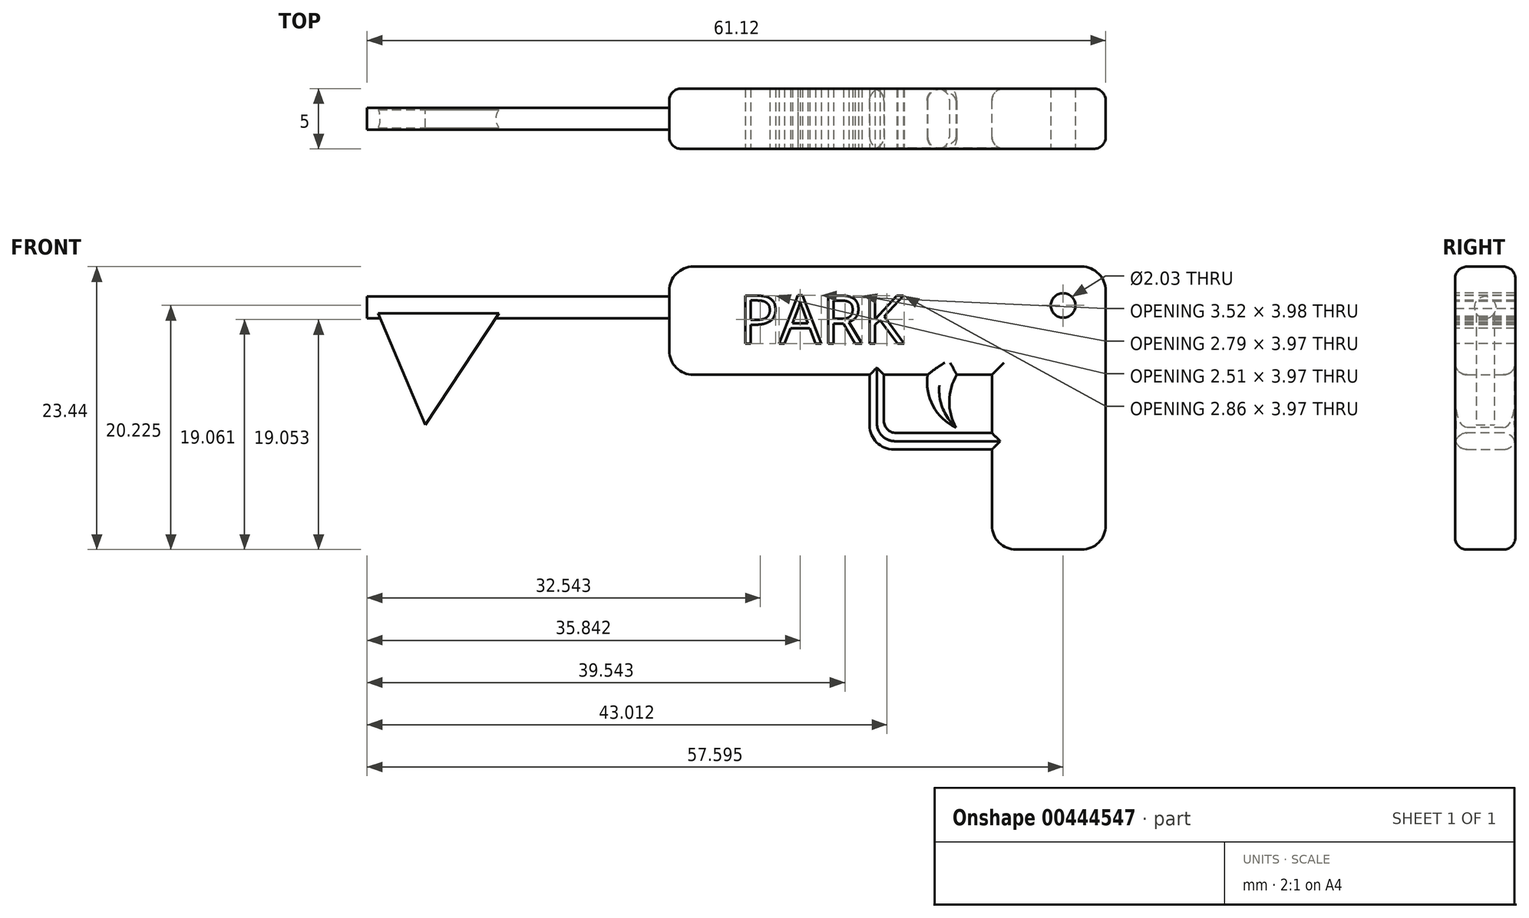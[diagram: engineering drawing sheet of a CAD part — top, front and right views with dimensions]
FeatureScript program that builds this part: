
annotation { "Feature Type Name" : "Feature", "Feature Type Description" : "" }
export const myFeature = defineFeature(function(context is Context, id is Id, definition is map)
    precondition{}
    {
        {
            var Q0;
            Q0=qCreatedBy(makeId("Front.planeOp"),FACE);
            var sketch = newSketch(context, id + "F0", { "sketchPlane" : qUnion([Q0])});
            skLineSegment(sketch, "E0", {"start": v(7.32, -12.37) * mm, "end": v(12.73, -12.37) * mm});
            skLineSegment(sketch, "E1", {"start": v(14.73, -10.37) * mm, "end": v(14.73, 9.07) * mm});
            skLineSegment(sketch, "E2", {"start": v(12.73, 11.07) * mm, "end": v(-19.39, 11.07) * mm});
            skLineSegment(sketch, "E3", {"start": v(-21.39, 9.07) * mm, "end": v(-21.39, 4.1) * mm});
            skLineSegment(sketch, "E4", {"start": v(-19.39, 2.1) * mm, "end": v(-4.8, 2.1) * mm});
            skLineSegment(sketch, "E5", {"start": v(-4.8, 2.1) * mm, "end": v(-4.8, -2.08) * mm});
            skLineSegment(sketch, "E6", {"start": v(-2.8, -4.08) * mm, "end": v(5.32, -4.08) * mm});
            skLineSegment(sketch, "E7", {"start": v(5.32, -4.08) * mm, "end": v(5.32, -10.37) * mm});
            skPoint(sketch, "E8.visualSharp", {"position": v(-21.39, 11.07) * mm});
            skArc(sketch, "E8.filletArc", {"start": v(-19.39, 11.07) * mm, "mid": v(-20.8, 10.48) * mm, "end": v(-21.39, 9.07) * mm});
            skPoint(sketch, "E9.visualSharp", {"position": v(-21.39, 2.1) * mm});
            skArc(sketch, "E9.filletArc", {"start": v(-21.39, 4.1) * mm, "mid": v(-20.8, 2.7) * mm, "end": v(-19.39, 2.1) * mm});
            skPoint(sketch, "E10.visualSharp", {"position": v(14.73, 11.07) * mm});
            skArc(sketch, "E10.filletArc", {"start": v(14.73, 9.07) * mm, "mid": v(14.15, 10.48) * mm, "end": v(12.73, 11.07) * mm});
            skPoint(sketch, "E11.visualSharp", {"position": v(14.73, -12.37) * mm});
            skArc(sketch, "E11.filletArc", {"start": v(12.73, -12.37) * mm, "mid": v(14.15, -11.78) * mm, "end": v(14.73, -10.37) * mm});
            skPoint(sketch, "E12.visualSharp", {"position": v(5.32, -12.37) * mm});
            skArc(sketch, "E12.filletArc", {"start": v(5.32, -10.37) * mm, "mid": v(5.9, -11.78) * mm, "end": v(7.32, -12.37) * mm});
            skPoint(sketch, "E13.visualSharp", {"position": v(-4.8, -4.08) * mm});
            skArc(sketch, "E13.filletArc", {"start": v(-4.8, -2.08) * mm, "mid": v(-4.22, -3.49) * mm, "end": v(-2.8, -4.08) * mm});
            skSolve(sketch);
        }
        {
            var Q0;
            Q0 = qSketchRegion(id + "F0", true);
            extrude(context, id + "F1", {"entities" : qUnion([Q0]), "depth" : 5 * mm});
        }
        {
            var Q0;
            Q0=makeQuery(id+"F1.opExtrude","CAP_FACE",FACE,{"disambiguationData":[OSD([sQuery(id+"F0.wireOp",EDGE,"E0"),sQuery(id+"F0.wireOp",EDGE,"E1"),sQuery(id+"F0.wireOp",EDGE,"E2"),sQuery(id+"F0.wireOp",EDGE,"E3"),sQuery(id+"F0.wireOp",EDGE,"E4"),sQuery(id+"F0.wireOp",EDGE,"E5"),sQuery(id+"F0.wireOp",EDGE,"E6"),sQuery(id+"F0.wireOp",EDGE,"E7"),sQuery(id+"F0.wireOp",EDGE,"E8.filletArc"),sQuery(id+"F0.wireOp",EDGE,"E9.filletArc"),sQuery(id+"F0.wireOp",EDGE,"E10.filletArc"),sQuery(id+"F0.wireOp",EDGE,"E11.filletArc"),sQuery(id+"F0.wireOp",EDGE,"E12.filletArc"),sQuery(id+"F0.wireOp",EDGE,"E13.filletArc")])],"isStart":false});
            var sketch = newSketch(context, id + "F2", { "sketchPlane" : qUnion([Q0])});
            skLineSegment(sketch, "E14.bottom", {"start": v(-3.62, 2.1) * mm, "end": v(0, 2.1) * mm});
            skLineSegment(sketch, "E14.top", {"start": v(-2.62, -2.7) * mm, "end": v(5.32, -2.7) * mm});
            skLineSegment(sketch, "E14.left", {"start": v(-3.62, 2.1) * mm, "end": v(-3.62, -1.7) * mm});
            skLineSegment(sketch, "E14.right", {"start": v(5.32, 2.1) * mm, "end": v(5.32, -2.7) * mm});
            skPoint(sketch, "E15.visualSharp", {"position": v(-3.62, -2.7) * mm});
            skArc(sketch, "E15.filletArc", {"start": v(-3.62, -1.7) * mm, "mid": v(-3.33, -2.41) * mm, "end": v(-2.62, -2.7) * mm});
            skArc(sketch, "E16", {"start": v(2.4, 2.1) * mm, "mid": v(1.79, -0.06) * mm, "end": v(2.33, -2.26) * mm});
            skArc(sketch, "E17", {"start": v(0, 2.1) * mm, "mid": v(0.44, -0.47) * mm, "end": v(2.33, -2.26) * mm});
            skLineSegment(sketch, "E18.trimOffspring", {"start": v(2.4, 2.1) * mm, "end": v(5.32, 2.1) * mm});
            skSolve(sketch);
        }
        {
            var Q0;
            Q0 = qSketchRegion(id + "F2", true);
            extrude(context, id + "F3", {"entities" : qUnion([Q0]), "operationType" : NewBodyOperationType.REMOVE, "endBound" : BoundingType.THROUGH_ALL, "oppositeDirection" : true, "depth" : 25 * mm});
        }
        {
            var Q0;
            Q0=makeQuery(id+"F1.opExtrude","CAP_EDGE",EDGE,{"disambiguationData":[OSD([sQuery(id+"F0.wireOp",EDGE,"E2")])],"isStart":false});
            var Q1;
            Q1=makeQuery(id+"F1.opExtrude","CAP_FACE",FACE,{"disambiguationData":[OSD([sQuery(id+"F0.wireOp",EDGE,"E0"),sQuery(id+"F0.wireOp",EDGE,"E1"),sQuery(id+"F0.wireOp",EDGE,"E2"),sQuery(id+"F0.wireOp",EDGE,"E3"),sQuery(id+"F0.wireOp",EDGE,"E4"),sQuery(id+"F0.wireOp",EDGE,"E5"),sQuery(id+"F0.wireOp",EDGE,"E6"),sQuery(id+"F0.wireOp",EDGE,"E7"),sQuery(id+"F0.wireOp",EDGE,"E8.filletArc"),sQuery(id+"F0.wireOp",EDGE,"E9.filletArc"),sQuery(id+"F0.wireOp",EDGE,"E10.filletArc"),sQuery(id+"F0.wireOp",EDGE,"E11.filletArc"),sQuery(id+"F0.wireOp",EDGE,"E12.filletArc"),sQuery(id+"F0.wireOp",EDGE,"E13.filletArc")])],"isStart":true});
            var Q2;
            Q2=makeQuery(id+"F1.opExtrude","CAP_FACE",FACE,{"disambiguationData":[OSD([sQuery(id+"F0.wireOp",EDGE,"E0"),sQuery(id+"F0.wireOp",EDGE,"E1"),sQuery(id+"F0.wireOp",EDGE,"E2"),sQuery(id+"F0.wireOp",EDGE,"E3"),sQuery(id+"F0.wireOp",EDGE,"E4"),sQuery(id+"F0.wireOp",EDGE,"E5"),sQuery(id+"F0.wireOp",EDGE,"E6"),sQuery(id+"F0.wireOp",EDGE,"E7"),sQuery(id+"F0.wireOp",EDGE,"E8.filletArc"),sQuery(id+"F0.wireOp",EDGE,"E9.filletArc"),sQuery(id+"F0.wireOp",EDGE,"E10.filletArc"),sQuery(id+"F0.wireOp",EDGE,"E11.filletArc"),sQuery(id+"F0.wireOp",EDGE,"E12.filletArc"),sQuery(id+"F0.wireOp",EDGE,"E13.filletArc")])],"isStart":false});
            fillet(context, id + "F4", {"entities" : qUnion([Q0, Q1, Q2]), "radius" : 1 * mm, "tangentPropagation" : true, "allowEdgeOverflow" : false});
        }
        {
            var Q0;
            Q0=makeQuery(id+"F1.opExtrude","CAP_FACE",FACE,{"disambiguationData":[OSD([sQuery(id+"F0.wireOp",EDGE,"E0"),sQuery(id+"F0.wireOp",EDGE,"E1"),sQuery(id+"F0.wireOp",EDGE,"E2"),sQuery(id+"F0.wireOp",EDGE,"E3"),sQuery(id+"F0.wireOp",EDGE,"E4"),sQuery(id+"F0.wireOp",EDGE,"E5"),sQuery(id+"F0.wireOp",EDGE,"E6"),sQuery(id+"F0.wireOp",EDGE,"E7"),sQuery(id+"F0.wireOp",EDGE,"E8.filletArc"),sQuery(id+"F0.wireOp",EDGE,"E9.filletArc"),sQuery(id+"F0.wireOp",EDGE,"E10.filletArc"),sQuery(id+"F0.wireOp",EDGE,"E11.filletArc"),sQuery(id+"F0.wireOp",EDGE,"E12.filletArc"),sQuery(id+"F0.wireOp",EDGE,"E13.filletArc")])],"isStart":false});
            var sketch = newSketch(context, id + "F5", { "sketchPlane" : qUnion([Q0])});
            skCircle(sketch, "E19", {"center": v(11.2, 7.86) * mm, "radius": 1.02 * mm});
            skSolve(sketch);
        }
        {
            var Q0;
            Q0 = qSketchRegion(id + "F5", true);
            extrude(context, id + "F6", {"entities" : qUnion([Q0]), "operationType" : NewBodyOperationType.REMOVE, "endBound" : BoundingType.THROUGH_ALL, "oppositeDirection" : true, "depth" : 25 * mm});
        }
        {
            var Q0;
            Q0=makeQuery(id+"F1.opExtrude","CAP_FACE",FACE,{"disambiguationData":[OSD([sQuery(id+"F0.wireOp",EDGE,"E0"),sQuery(id+"F0.wireOp",EDGE,"E1"),sQuery(id+"F0.wireOp",EDGE,"E2"),sQuery(id+"F0.wireOp",EDGE,"E3"),sQuery(id+"F0.wireOp",EDGE,"E4"),sQuery(id+"F0.wireOp",EDGE,"E5"),sQuery(id+"F0.wireOp",EDGE,"E6"),sQuery(id+"F0.wireOp",EDGE,"E7"),sQuery(id+"F0.wireOp",EDGE,"E8.filletArc"),sQuery(id+"F0.wireOp",EDGE,"E9.filletArc"),sQuery(id+"F0.wireOp",EDGE,"E10.filletArc"),sQuery(id+"F0.wireOp",EDGE,"E11.filletArc"),sQuery(id+"F0.wireOp",EDGE,"E12.filletArc"),sQuery(id+"F0.wireOp",EDGE,"E13.filletArc")])],"isStart":false});
            var sketch = newSketch(context, id + "F7", { "sketchPlane" : qUnion([Q0])});
            skText(sketch, "E20", { "text": "PARK", "fontName": "OpenSans-Regular.ttf"});
            const initialGuessF7  = {"E20": [-0.01565, 0.0047, 1, 0, 0.004]};
            skSetInitialGuess(sketch, initialGuessF7);
            skSolve(sketch);
        }
        {
            var Q0;
            Q0 = qSketchRegion(id + "F7", true);
            extrude(context, id + "F8", {"entities" : qUnion([Q0]), "operationType" : NewBodyOperationType.REMOVE, "oppositeDirection" : true, "depth" : 25 * mm});
        }
        {
            var Q0;
            Q0=makeQuery(id+"F1.opExtrude","SWEPT_FACE",FACE,{"disambiguationData":[OSD([sQuery(id+"F0.wireOp",EDGE,"E3")])]});
            var sketch = newSketch(context, id + "F9", { "sketchPlane" : qUnion([Q0])});
            skCircle(sketch, "E21", {"center": v(2.5, 7.69) * mm, "radius": 0.9 * mm});
            skSolve(sketch);
        }
        {
            var Q0;
            Q0 = qSketchRegion(id + "F9", true);
            extrude(context, id + "F10", {"entities" : qUnion([Q0]), "operationType" : NewBodyOperationType.ADD, "depth" : 25 * mm});
        }
        {
            var Q0;
            Q0=qCreatedBy(makeId("Front.planeOp"),FACE);
            cPlane(context, id + "F11", {"entities" : qUnion([Q0]), "cplaneType" : CPlaneType.OFFSET, "offset" : 2.5 * mm, "width" : 150 * mm, "height" : 150 * mm});
        }
        {
            var Q0;
            Q0=qCreatedBy(id+"F11.planeOp",FACE);
            var sketch = newSketch(context, id + "F12", { "sketchPlane" : qUnion([Q0])});
            skLineSegment(sketch, "E22", {"start": v(-40.05, 7.52) * mm, "end": v(-45.61, 7.52) * mm});
            skLineSegment(sketch, "E23", {"start": v(-45.61, 7.52) * mm, "end": v(-41.56, -2.05) * mm});
            skLineSegment(sketch, "E24", {"start": v(-41.56, -2.05) * mm, "end": v(-35.25, 7.52) * mm});
            skLineSegment(sketch, "E25", {"start": v(-35.25, 7.52) * mm, "end": v(-40.05, 7.52) * mm});
            skSolve(sketch);
        }
        {
            var Q0;
            Q0 = qSketchRegion(id + "F12", true);
            extrude(context, id + "F13", {"entities" : qUnion([Q0]), "operationType" : NewBodyOperationType.ADD, "endBound" : BoundingType.SYMMETRIC, "depth" : 1.5 * mm});
        }
    });
